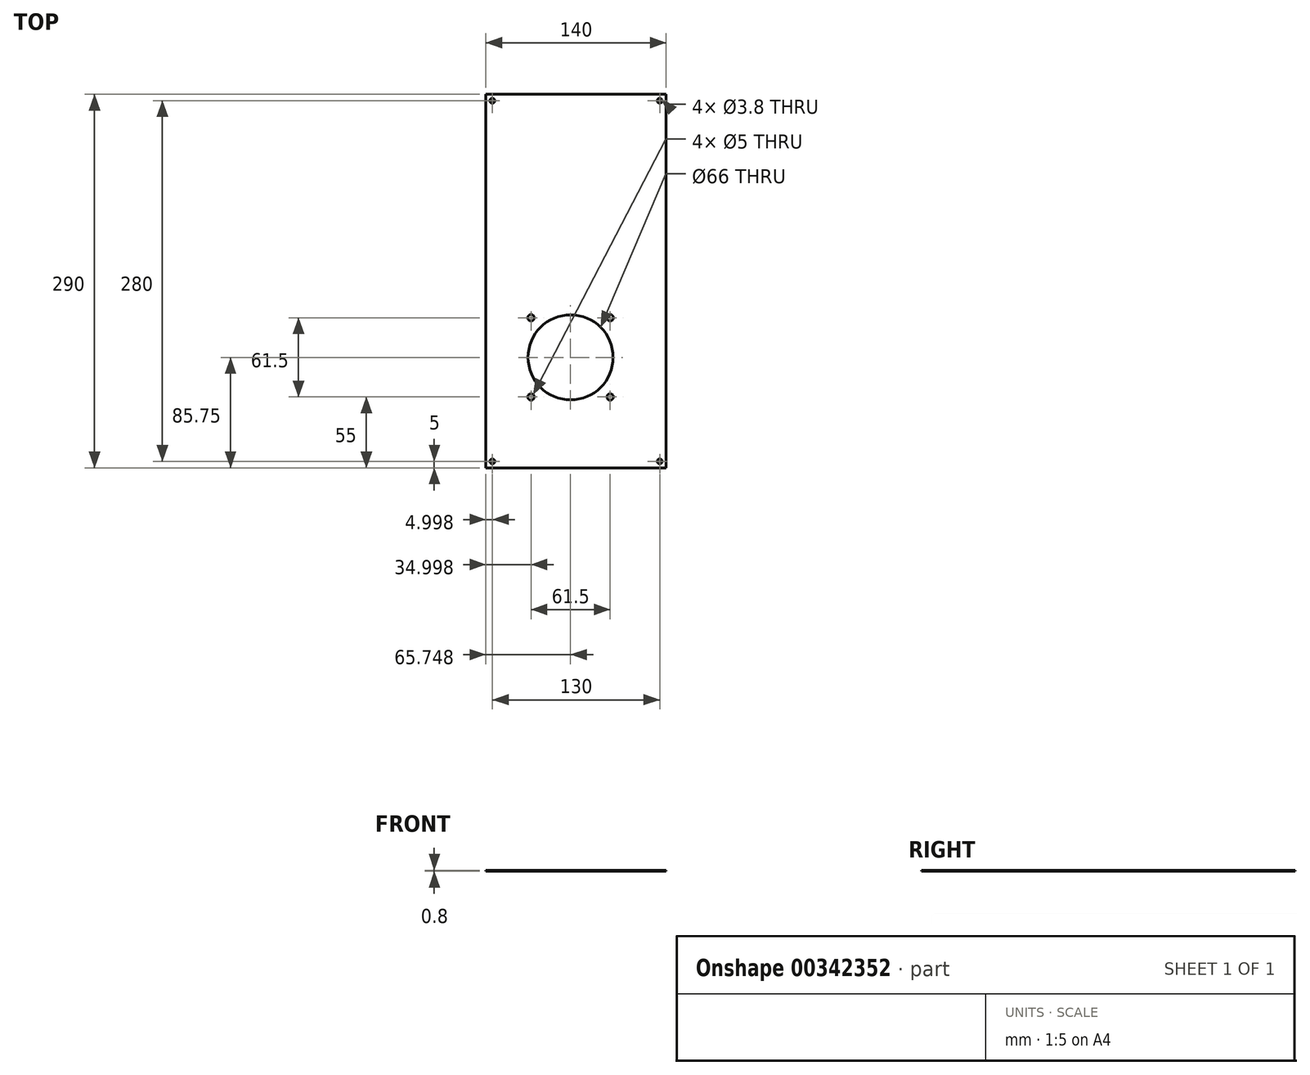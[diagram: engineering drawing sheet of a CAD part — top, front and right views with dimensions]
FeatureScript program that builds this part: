
annotation { "Feature Type Name" : "Feature", "Feature Type Description" : "" }
export const myFeature = defineFeature(function(context is Context, id is Id, definition is map)
    precondition{}
    {
        {
            var Q0;
            Q0=qCreatedBy(makeId("Top.planeOp"),FACE);
            var sketch = newSketch(context, id + "F0", { "sketchPlane" : qUnion([Q0])});
            skLineSegment(sketch, "E0.bottom", {"start": v(-743.6, -475.32) * mm, "end": v(-603.6, -475.32) * mm});
            skLineSegment(sketch, "E0.top", {"start": v(-743.6, -765.32) * mm, "end": v(-603.6, -765.32) * mm});
            skLineSegment(sketch, "E0.left", {"start": v(-743.6, -475.32) * mm, "end": v(-743.6, -765.32) * mm});
            skLineSegment(sketch, "E0.right", {"start": v(-603.6, -475.32) * mm, "end": v(-603.6, -765.32) * mm});
            skCircle(sketch, "E1", {"center": v(-608.6, -760.32) * mm, "radius": 1.9 * mm});
            skCircle(sketch, "E2", {"center": v(-738.6, -760.32) * mm, "radius": 1.9 * mm});
            skCircle(sketch, "E3", {"center": v(-608.6, -480.32) * mm, "radius": 1.9 * mm});
            skCircle(sketch, "E4", {"center": v(-738.6, -480.32) * mm, "radius": 1.9 * mm});
            skCircle(sketch, "E5", {"center": v(-708.6, -648.82) * mm, "radius": 2.5 * mm});
            skCircle(sketch, "E6", {"center": v(-708.6, -710.32) * mm, "radius": 2.5 * mm});
            skCircle(sketch, "E7", {"center": v(-647.1, -648.82) * mm, "radius": 2.5 * mm});
            skCircle(sketch, "E8", {"center": v(-647.1, -710.32) * mm, "radius": 2.5 * mm});
            skCircle(sketch, "E9", {"center": v(-677.85, -679.57) * mm, "radius": 33 * mm});
            skSolve(sketch);
        }
        {
            var Q0;
            Q0 = qSketchRegion(id + "F0", true);
            extrude(context, id + "F1", {"entities" : qUnion([Q0]), "depth" : 0.8 * mm});
        }
    });
